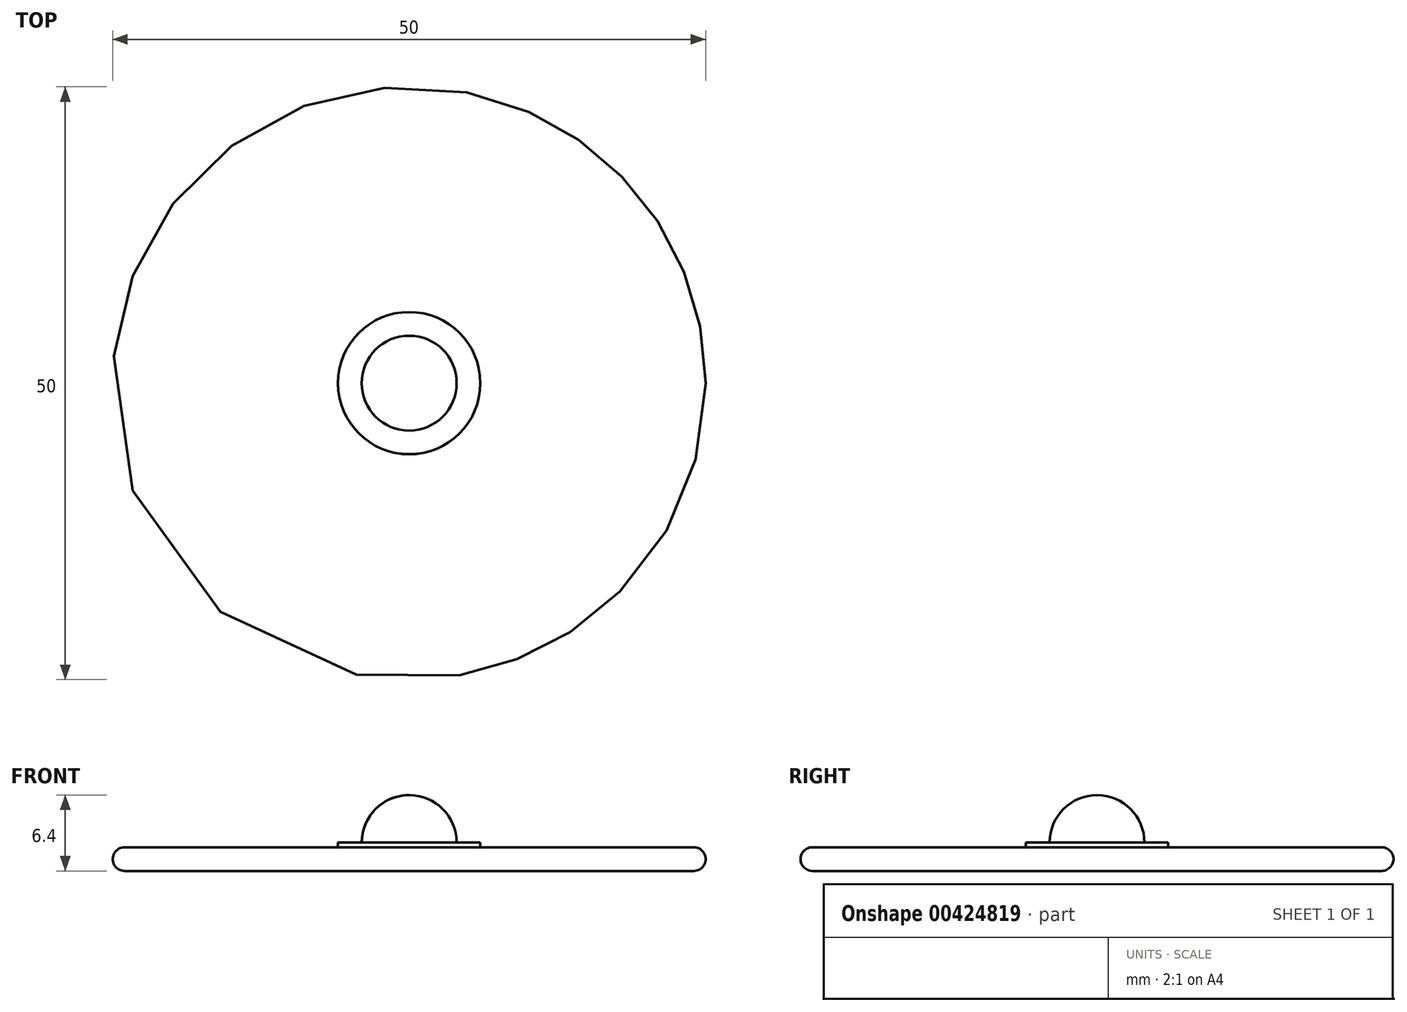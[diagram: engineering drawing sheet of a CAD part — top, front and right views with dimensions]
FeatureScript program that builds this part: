
annotation { "Feature Type Name" : "Feature", "Feature Type Description" : "" }
export const myFeature = defineFeature(function(context is Context, id is Id, definition is map)
    precondition{}
    {
        {
            var Q0;
            Q0=qCreatedBy(makeId("Front.planeOp"),FACE);
            var sketch = newSketch(context, id + "F0", { "sketchPlane" : qUnion([Q0])});
            skArc(sketch, "E0", {"start": v(-24, 2) * mm, "mid": v(-25, 1) * mm, "end": v(-24, 0) * mm});
            skLineSegment(sketch, "E1", {"start": v(-24, 0) * mm, "end": v(0, 0) * mm});
            skLineSegment(sketch, "E2", {"start": v(0, 2) * mm, "end": v(0, 0) * mm});
            skLineSegment(sketch, "E3", {"start": v(0, 2) * mm, "end": v(-24, 2) * mm});
            skSolve(sketch);
        }
        {
            var Q0;
            Q0=makeQuery(id+"F0.imprint","IMPRINT",FACE,{"disambiguationData":[TD([[makeQuery(id+"F0.imprint","IMPRINT",EDGE,{"derivedFrom":sQuery(id+"F0.wireOp",EDGE,"E0")}),1.0]])]});
            var Q1;
            Q1 = qSketchRegion(id + "F2", true);
            var Q2;
            Q2=sQuery(id+"F0.wireOp",EDGE,"E2");
            revolve(context, id + "F1", {"entities" : qUnion([Q0, Q1]), "axis" : qUnion([Q2]), "revolveType" : RevolveType.FULL});
        }
        {
            var Q0;
            Q0=qCreatedBy(makeId("Front.planeOp"),FACE);
            var sketch = newSketch(context, id + "F2", { "sketchPlane" : qUnion([Q0])});
            skArc(sketch, "E4", {"start": v(0, 6.4) * mm, "mid": v(-2.83, 5.23) * mm, "end": v(-4, 2.4) * mm});
            skLineSegment(sketch, "E5", {"start": v(-6, 2.4) * mm, "end": v(-4, 2.4) * mm});
            skLineSegment(sketch, "E6", {"start": v(-6, 2) * mm, "end": v(0, 2) * mm});
            skLineSegment(sketch, "E7", {"start": v(-6, 2.4) * mm, "end": v(-6, 2) * mm});
            skLineSegment(sketch, "E8", {"start": v(0, 2.4) * mm, "end": v(0, 6.4) * mm});
            skLineSegment(sketch, "E9", {"start": v(0, 2.4) * mm, "end": v(0, 2) * mm});
            skSolve(sketch);
        }
        {
            var Q0;
            Q0=makeQuery(id+"F2.imprint","IMPRINT",FACE,{"disambiguationData":[TD([[makeQuery(id+"F2.imprint","IMPRINT",EDGE,{"derivedFrom":sQuery(id+"F2.wireOp",EDGE,"E4")}),1.0]])]});
            var Q1;
            Q1=sQuery(id+"F2.wireOp",EDGE,"E8");
            revolve(context, id + "F3", {"entities" : qUnion([Q0]), "axis" : qUnion([Q1]), "revolveType" : RevolveType.FULL});
        }
    });
